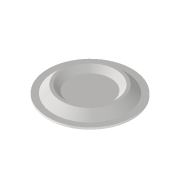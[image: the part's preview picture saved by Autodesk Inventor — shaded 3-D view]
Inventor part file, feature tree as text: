
AUTODESK INVENTOR PART (.ipt)
format: ipt  version: 2022 (Build 260153000, 153)  size: 130,560 bytes
history: native  units: mm
features: revolve x1, sketch x1
ambient origin geometry x8: Origin, YZ Plane, XZ Plane, XY Plane, X Axis, Y Axis, Z Axis, Center Point
bodies: Volumenkörper1 (feature_tree)
feature tree (2):
  revolve  "Umdrehung1"
  sketch  "Skizze1"  dims[d14=0.125mm d15=12.0mm d16=0.3mm d18=135.0deg d20=0.2mm d27=135.0deg d28=1.0mm d29=1.2mm d30=0.6mm d31=0.6mm d34=1.0mm d36=0.6mm d37=12.5mm d38=90.0deg]
